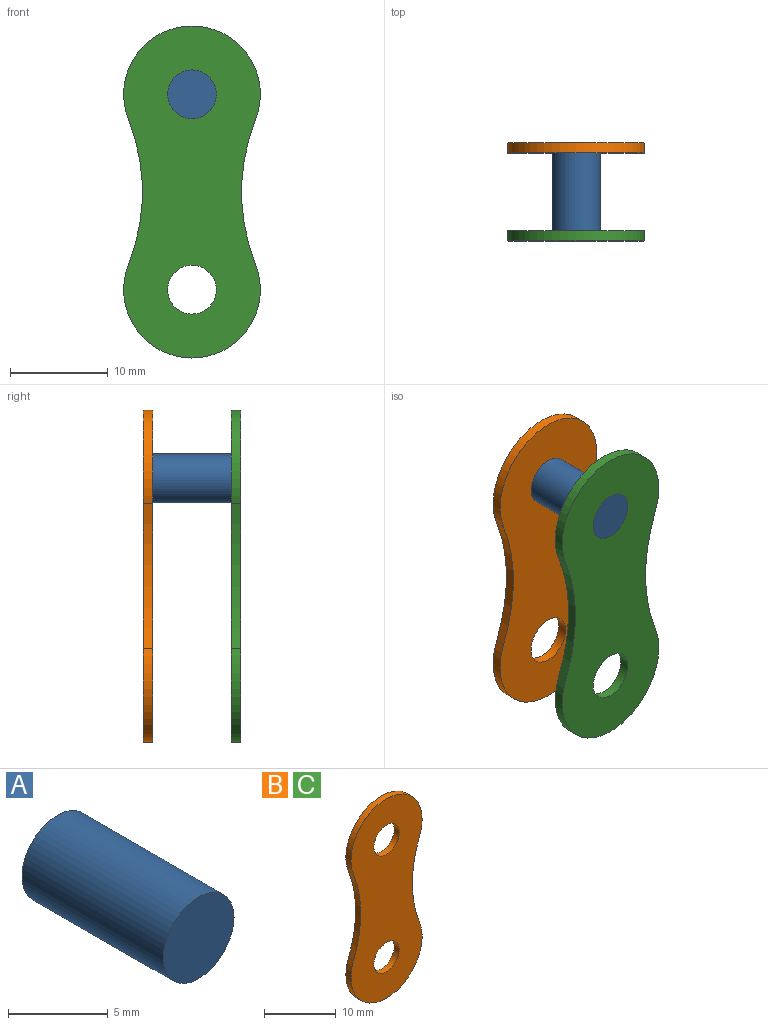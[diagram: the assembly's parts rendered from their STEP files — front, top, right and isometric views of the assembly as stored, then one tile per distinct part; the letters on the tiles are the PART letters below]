
ASSEMBLY  parts=3 mates=2
PART A: 3 faces, bbox 5x10x5 mm
  f0: cylinder r=2.5mm len=10mm, axis (0,1,0), area 157.1mm2, adj f1,f2
  f1: plane 5x5mm, normal (0,-1,0), area 19.6mm2, adj f0
  f2: plane 5x5mm, normal (0,1,0), area 19.6mm2, adj f0
PART B: 8 faces, bbox 14x1x34 mm
  f0: cylinder r=20mm len=14.82mm, axis (0,1,0), area 15.2mm2, adj f1,f5,f6,f7
  f1: cylinder r=7mm len=14mm, axis (0,1,0), area 27.3mm2, adj f0,f2,f6,f7
  f2: cylinder r=20mm len=14.82mm, axis (0,1,0), area 15.2mm2, adj f1,f5,f6,f7
  f3: cylinder r=2.5mm len=5mm, axis (0,1,0), area 15.7mm2, adj f6,f7
  f4: cylinder r=2.5mm len=5mm, axis (0,1,0), area 15.7mm2, adj f6,f7
  f5: cylinder r=7mm len=14mm, axis (0,1,0), area 27.3mm2, adj f0,f2,f6,f7
  f6: plane 34x14mm, normal (0,-1,0), area 349.9mm2, adj f0,f1,f2,f3,f4,f5
  f7: plane 34x14mm, normal (0,1,0), area 349.9mm2, adj f0,f1,f2,f3,f4,f5
PART C: same geometry as B
PLACE A t=(11.63,11.46,-17.36)mm
PLACE B t=(29.19,11.46,-27.56)mm
PLACE C t=(29.19,2.46,-27.56)mm
MATE fastened A.f0 <-> B.f3  axis (0,1,0) through (-16.42,11.46,40.66)mm
MATE fastened A.f0 <-> C.f3  axis (0,-1,0) through (-16.42,1.46,40.66)mm
